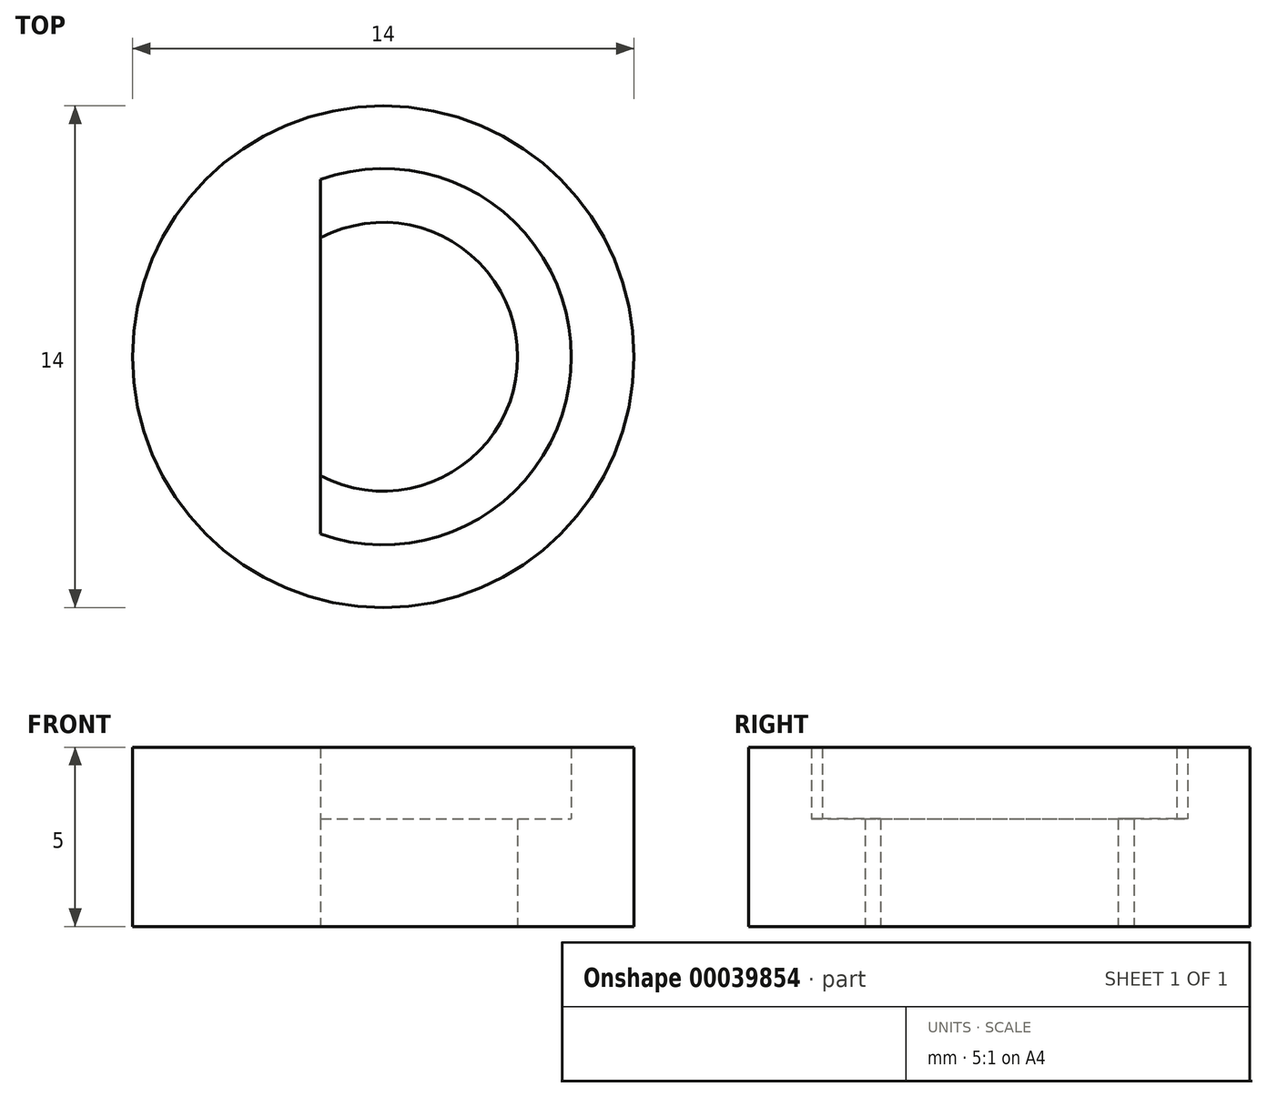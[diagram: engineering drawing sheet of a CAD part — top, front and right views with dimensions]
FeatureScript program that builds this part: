
annotation { "Feature Type Name" : "Feature", "Feature Type Description" : "" }
export const myFeature = defineFeature(function(context is Context, id is Id, definition is map)
    precondition{}
    {
        {
            var Q0;
            Q0=qCreatedBy(makeId("Top.planeOp"),FACE);
            var sketch = newSketch(context, id + "F0", { "sketchPlane" : qUnion([Q0])});
            skCircle(sketch, "E0", {"center": v(0, 0) * mm, "radius": 3.75 * mm});
            skCircle(sketch, "E1", {"center": v(0, 0) * mm, "radius": 5.25 * mm});
            skCircle(sketch, "E2", {"center": v(0, 0) * mm, "radius": 7 * mm});
            skLineSegment(sketch, "E3", {"start": v(3.75, 0) * mm, "end": v(-3.75, 0) * mm, "construction": true});
            skLineSegment(sketch, "E4", {"start": v(3.75, 0) * mm, "end": v(-1.75, 0) * mm});
            skLineSegment(sketch, "E5", {"start": v(-1.75, 4.95) * mm, "end": v(-1.75, -4.95) * mm});
            skSolve(sketch);
        }
        {
            var Q0;
            {var subQ0=sQuery(id+"F0.wireOp",EDGE,"E5");var subQ1=sQuery(id+"F0.wireOp",EDGE,"E0");var subQ4=makeQuery(id+"F0.imprint","INTERSECT",VERTEX,{"disambiguationData":[OD(0.0)],"derivedFrom":[subQ1,subQ0]});Q0=makeQuery(id+"F0.imprint","IMPRINT",FACE,{"disambiguationData":[TD([[makeQuery(id+"F0.imprint","IMPRINT",EDGE,{"disambiguationData":[TD([[subQ4,-1.0]])],"derivedFrom":subQ1}),1.0]])]});}
            var Q1;
            {var subQ0=sQuery(id+"F0.wireOp",EDGE,"E5");var subQ1=sQuery(id+"F0.wireOp",EDGE,"E0");var subQ5=makeQuery(id+"F0.imprint","INTERSECT",VERTEX,{"disambiguationData":[OD(0.0)],"derivedFrom":[subQ1,subQ0]});Q1=makeQuery(id+"F0.imprint","IMPRINT",FACE,{"disambiguationData":[TD([[makeQuery(id+"F0.imprint","IMPRINT",EDGE,{"disambiguationData":[TD([[subQ5,-1.0]])],"derivedFrom":subQ1}),-1.0]])]});}
            var Q2;
            Q2=makeQuery(id+"F0.imprint","IMPRINT",FACE,{"disambiguationData":[TD([[makeQuery(id+"F0.imprint","IMPRINT",EDGE,{"derivedFrom":sQuery(id+"F0.wireOp",EDGE,"E2")}),1.0]])]});
            extrude(context, id + "F1", {"entities" : qUnion([Q0, Q1, Q2]), "depth" : 5 * mm});
        }
        {
            var Q0;
            {var subQ1=sQuery(id+"F0.wireOp",EDGE,"E0");var subQ6=makeQuery(id+"F0.imprint","INTERSECT",VERTEX,{"derivedFrom":[subQ1,sQuery(id+"F0.wireOp",EDGE,"E4")]});Q0=makeQuery(id+"F0.imprint","IMPRINT",FACE,{"disambiguationData":[TD([[makeQuery(id+"F0.imprint","IMPRINT",EDGE,{"disambiguationData":[TD([[subQ6,-1.0]])],"derivedFrom":subQ1}),-1.0]])]});}
            extrude(context, id + "F2", {"entities" : qUnion([Q0]), "operationType" : NewBodyOperationType.ADD, "depth" : 3 * mm});
        }
    });
